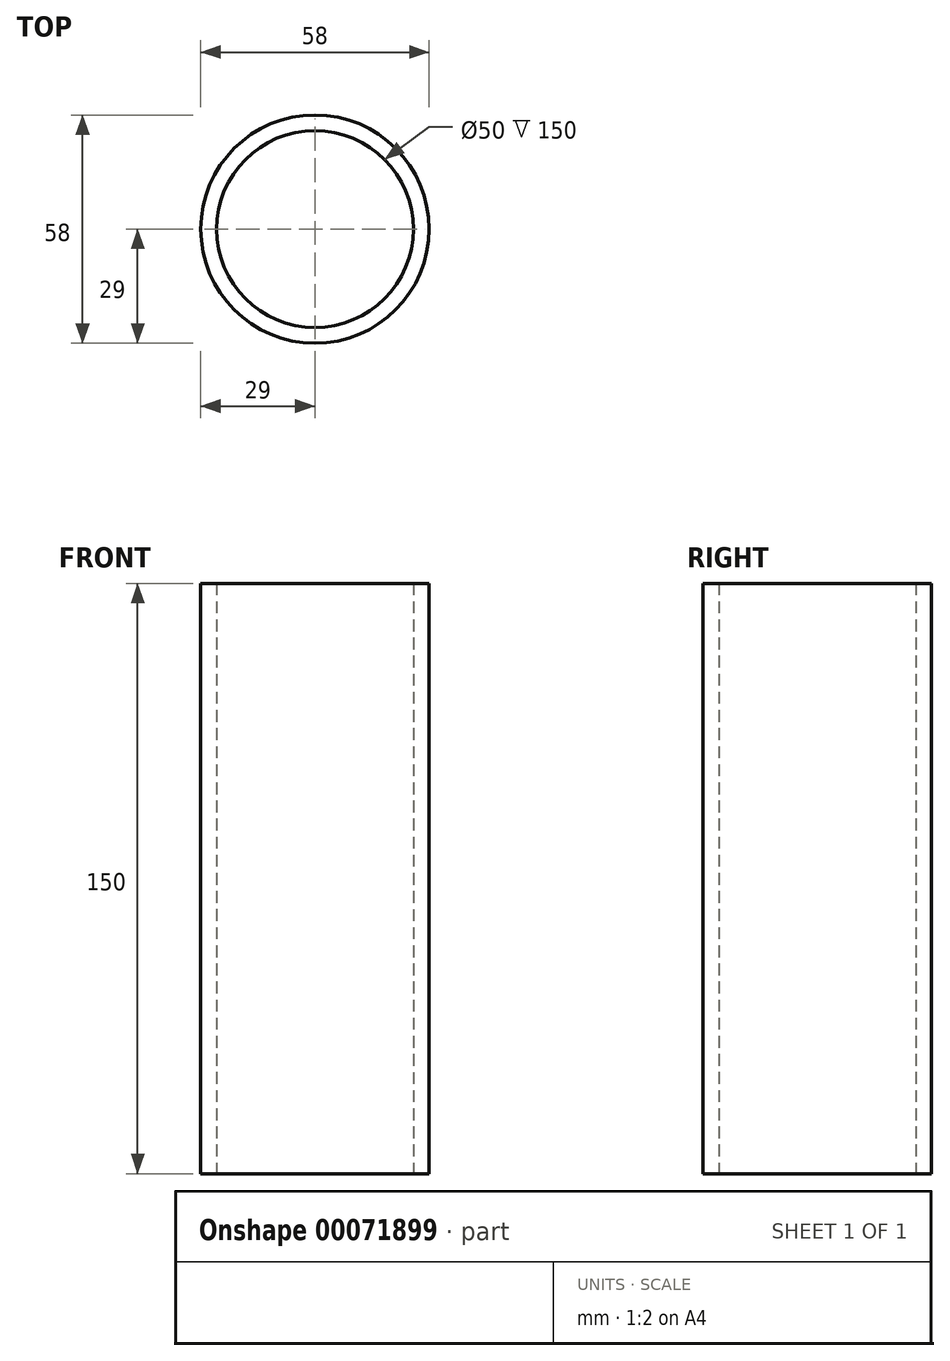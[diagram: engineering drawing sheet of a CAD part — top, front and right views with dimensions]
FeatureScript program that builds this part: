
annotation { "Feature Type Name" : "Feature", "Feature Type Description" : "" }
export const myFeature = defineFeature(function(context is Context, id is Id, definition is map)
    precondition{}
    {
        {
            var Q0;
            Q0=qCreatedBy(makeId("Top.planeOp"),FACE);
            var sketch = newSketch(context, id + "F0", { "sketchPlane" : qUnion([Q0])});
            skCircle(sketch, "E0", {"center": v(0, 0) * mm, "radius": 25 * mm});
            skCircle(sketch, "E1", {"center": v(0, 0) * mm, "radius": 29 * mm});
            skSolve(sketch);
        }
        {
            var Q0;
            Q0 = qSketchRegion(id + "F0", true);
            extrude(context, id + "F1", {"entities" : qUnion([Q0]), "depth" : 150 * mm});
        }
    });
